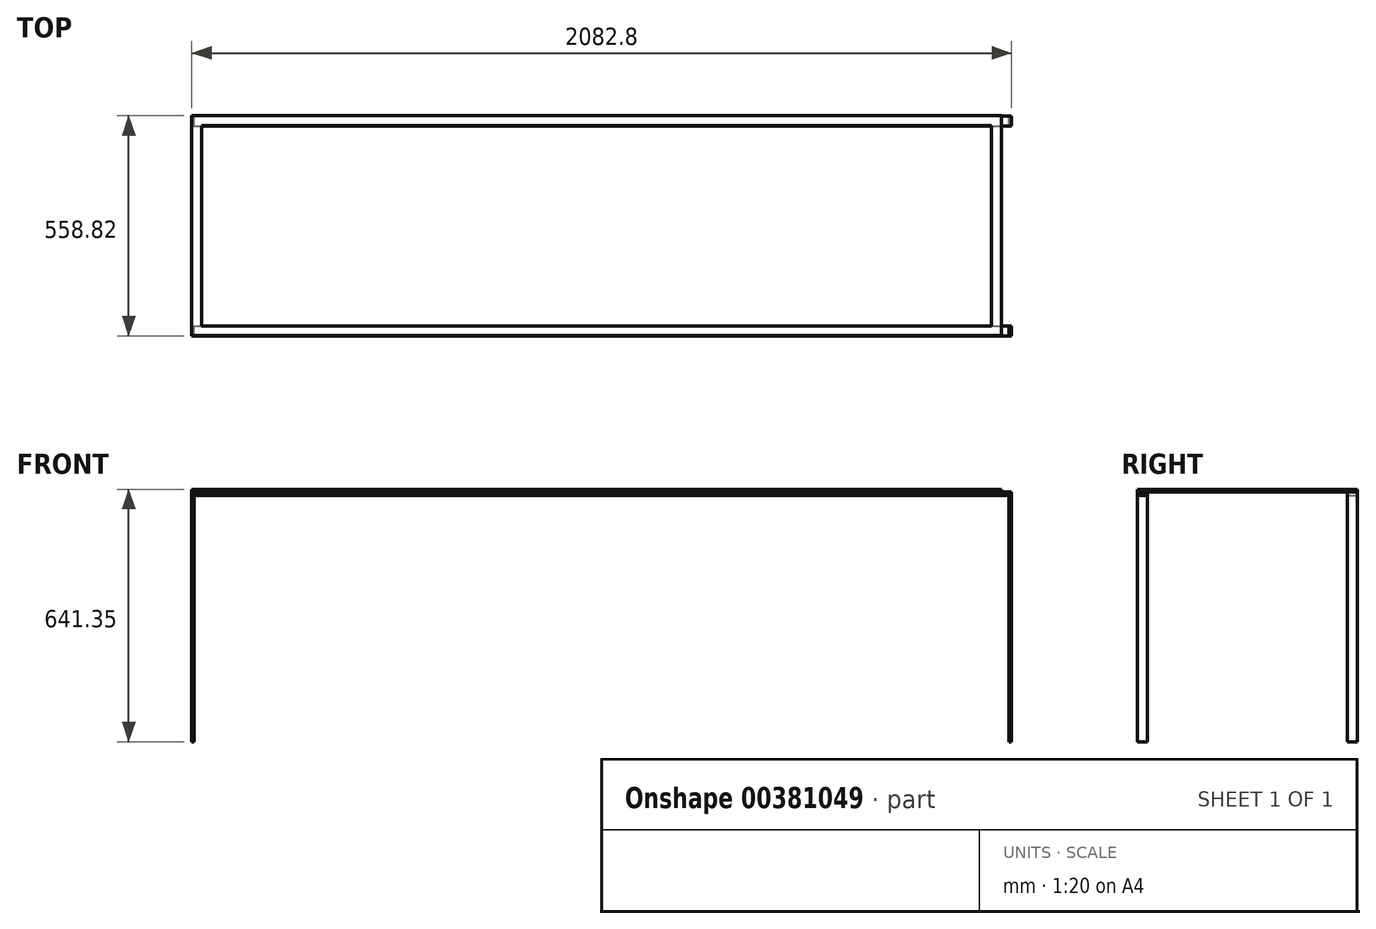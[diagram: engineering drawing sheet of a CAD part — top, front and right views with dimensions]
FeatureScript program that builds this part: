
annotation { "Feature Type Name" : "Feature", "Feature Type Description" : "" }
export const myFeature = defineFeature(function(context is Context, id is Id, definition is map)
    precondition{}
    {
        {
            var Q0;
            Q0=qCreatedBy(makeId("Front.planeOp"),FACE);
            var sketch = newSketch(context, id + "F0", { "sketchPlane" : qUnion([Q0])});
            skLineSegment(sketch, "E0.bottom", {"start": v(0, 0) * mm, "end": v(6.35, 0) * mm});
            skLineSegment(sketch, "E0.top", {"start": v(0, 635) * mm, "end": v(6.35, 635) * mm});
            skLineSegment(sketch, "E0.left", {"start": v(0, 0) * mm, "end": v(0, 635) * mm});
            skLineSegment(sketch, "E0.right", {"start": v(6.35, 0) * mm, "end": v(6.35, 635) * mm});
            skLineSegment(sketch, "E1.left", {"start": v(0, 635) * mm, "end": v(0, 625.47) * mm});
            skLineSegment(sketch, "E1.right", {"start": v(2082.8, 635) * mm, "end": v(2082.8, 625.48) * mm});
            skLineSegment(sketch, "E2.bottom", {"start": v(2082.8, 635) * mm, "end": v(2076.45, 635) * mm});
            skLineSegment(sketch, "E2.top", {"start": v(2082.8, 0) * mm, "end": v(2076.45, 0) * mm});
            skLineSegment(sketch, "E2.left", {"start": v(2082.8, 635) * mm, "end": v(2082.8, 0) * mm});
            skLineSegment(sketch, "E2.right", {"start": v(2076.45, 635) * mm, "end": v(2076.45, 0) * mm});
            skLineSegment(sketch, "E3.bottom", {"start": v(0, 625.47) * mm, "end": v(2082.8, 625.47) * mm});
            skLineSegment(sketch, "E3.top", {"start": v(0, 635) * mm, "end": v(2082.8, 635) * mm});
            skLineSegment(sketch, "E3.left", {"start": v(0, 625.47) * mm, "end": v(0, 635) * mm});
            skLineSegment(sketch, "E3.right", {"start": v(2082.8, 625.47) * mm, "end": v(2082.8, 635) * mm});
            skSolve(sketch);
        }
        {
            var Q0;
            {var subQ0=sQuery(id+"F0.wireOp",EDGE,"E3.top");var subQ1=sQuery(id+"F0.wireOp",EDGE,"E0.right");var subQ2=makeQuery(id+"F0.imprint","INTERSECT",VERTEX,{"derivedFrom":[subQ1,subQ0]});Q0=makeQuery(id+"F0.imprint","IMPRINT",FACE,{"disambiguationData":[TD([[makeQuery(id+"F0.imprint","IMPRINT",EDGE,{"disambiguationData":[TD([[subQ2,1.0]])],"derivedFrom":subQ1}),-1.0]])]});}
            var Q1;
            {var subQ0=sQuery(id+"F0.wireOp",EDGE,"E0.bottom");Q1=makeQuery(id+"F0.imprint","IMPRINT",FACE,{"disambiguationData":[TD([[makeQuery(id+"F0.imprint","IMPRINT",EDGE,{"derivedFrom":subQ0}),1.0]])]});}
            var Q2;
            {var subQ0=sQuery(id+"F0.wireOp",EDGE,"E2.top");Q2=makeQuery(id+"F0.imprint","IMPRINT",FACE,{"disambiguationData":[TD([[makeQuery(id+"F0.imprint","IMPRINT",EDGE,{"derivedFrom":subQ0}),-1.0]])]});}
            extrude(context, id + "F1", {"entities" : qUnion([Q0, Q1, Q2]), "depth" : 25.4 * mm});
        }
        {
            var Q0;
            Q0=qCreatedBy(makeId("Top.planeOp"),FACE);
            cPlane(context, id + "F2", {"entities" : qUnion([Q0]), "cplaneType" : CPlaneType.OFFSET, "offset" : 635 * mm, "width" : 152.4 * mm, "height" : 152.4 * mm});
        }
        {
            var Q0;
            Q0=qCreatedBy(id+"F2.planeOp",FACE);
            var sketch = newSketch(context, id + "F3", { "sketchPlane" : qUnion([Q0])});
            skLineSegment(sketch, "E4.bottom", {"start": v(0, -25.38) * mm, "end": v(25.4, -25.38) * mm});
            skLineSegment(sketch, "E4.top", {"start": v(0, 533.42) * mm, "end": v(25.4, 533.42) * mm});
            skLineSegment(sketch, "E4.left", {"start": v(0, -25.38) * mm, "end": v(0, 533.42) * mm});
            skLineSegment(sketch, "E4.right", {"start": v(25.4, -25.38) * mm, "end": v(25.4, 533.42) * mm});
            skLineSegment(sketch, "E5.bottom", {"start": v(25.4, -25.38) * mm, "end": v(2057.4, -25.38) * mm});
            skLineSegment(sketch, "E5.top", {"start": v(25.4, 0) * mm, "end": v(2057.4, 0) * mm});
            skLineSegment(sketch, "E5.left", {"start": v(25.4, -25.38) * mm, "end": v(25.4, 0) * mm});
            skLineSegment(sketch, "E5.right", {"start": v(2057.4, -25.38) * mm, "end": v(2057.4, 0) * mm});
            skLineSegment(sketch, "E6.bottom", {"start": v(0, 533.42) * mm, "end": v(2057.4, 533.42) * mm});
            skLineSegment(sketch, "E6.top", {"start": v(0, 508.02) * mm, "end": v(2057.4, 508.02) * mm});
            skLineSegment(sketch, "E6.left", {"start": v(0, 533.42) * mm, "end": v(0, 508.02) * mm});
            skLineSegment(sketch, "E6.right", {"start": v(2057.4, 533.42) * mm, "end": v(2057.4, 508.02) * mm});
            skLineSegment(sketch, "E7.top", {"start": v(2073.28, -25.38) * mm, "end": v(2057.4, -25.38) * mm});
            skLineSegment(sketch, "E8.bottom", {"start": v(2057.4, 533.42) * mm, "end": v(2032, 533.42) * mm});
            skLineSegment(sketch, "E8.top", {"start": v(2057.4, -25.38) * mm, "end": v(2032, -25.38) * mm});
            skLineSegment(sketch, "E8.left", {"start": v(2057.4, 533.42) * mm, "end": v(2057.4, -25.38) * mm});
            skLineSegment(sketch, "E8.right", {"start": v(2032, 533.42) * mm, "end": v(2032, -25.38) * mm});
            skSolve(sketch);
        }
        {
            var Q0;
            Q0 = qSketchRegion(id + "F3", true);
            extrude(context, id + "F4", {"entities" : qUnion([Q0]), "operationType" : NewBodyOperationType.ADD, "depth" : 6.35 * mm});
        }
        {
            var Q0;
            Q0=qCreatedBy(makeId("Front.planeOp"),FACE);
            var Q1;
            Q1 = qBodyType(qCreatedBy(id + "F6" ,EDGE), BodyType.WIRE);
            cPlane(context, id + "F5", {"entities" : qUnion([Q0, Q1]), "cplaneType" : CPlaneType.OFFSET, "offset" : 533.4 * mm, "oppositeDirection" : true, "width" : 152.4 * mm, "height" : 152.4 * mm});
        }
        {
            var Q0;
            Q0=qCreatedBy(id+"F5.planeOp",FACE);
            var sketch = newSketch(context, id + "F6", { "sketchPlane" : qUnion([Q0])});
            skLineSegment(sketch, "E9.bottom", {"start": v(0, 0) * mm, "end": v(6.35, 0) * mm});
            skLineSegment(sketch, "E9.top", {"start": v(0, 635) * mm, "end": v(6.35, 635) * mm});
            skLineSegment(sketch, "E9.left", {"start": v(0, 0) * mm, "end": v(0, 635) * mm});
            skLineSegment(sketch, "E9.right", {"start": v(6.35, 0) * mm, "end": v(6.35, 635) * mm});
            skLineSegment(sketch, "E10.bottom", {"start": v(0, 635) * mm, "end": v(2082.8, 635) * mm});
            skLineSegment(sketch, "E10.top", {"start": v(0, 625.48) * mm, "end": v(2082.8, 625.48) * mm});
            skLineSegment(sketch, "E10.left", {"start": v(0, 635) * mm, "end": v(0, 625.48) * mm});
            skLineSegment(sketch, "E10.right", {"start": v(2082.8, 635) * mm, "end": v(2082.8, 625.48) * mm});
            skLineSegment(sketch, "E11.bottom", {"start": v(2082.8, 635) * mm, "end": v(2076.45, 635) * mm});
            skLineSegment(sketch, "E11.top", {"start": v(2082.8, 0) * mm, "end": v(2076.45, 0) * mm});
            skLineSegment(sketch, "E11.left", {"start": v(2082.8, 635) * mm, "end": v(2082.8, 0) * mm});
            skLineSegment(sketch, "E11.right", {"start": v(2076.45, 635) * mm, "end": v(2076.45, 0) * mm});
            skSolve(sketch);
        }
        {
            var Q0;
            Q0 = qSketchRegion(id + "F6", true);
            extrude(context, id + "F7", {"entities" : qUnion([Q0]), "operationType" : NewBodyOperationType.ADD, "depth" : 25.4 * mm});
        }
    });
